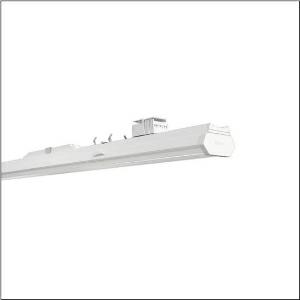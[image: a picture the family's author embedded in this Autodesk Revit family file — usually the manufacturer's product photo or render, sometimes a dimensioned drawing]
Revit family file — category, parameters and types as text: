
# Revit family: licross_21_protected_mo_52td127n485g
name_source: partatom
category: Lighting Fixtures
units: mm (PartAtom-declared; Revit-internal decimal feet)

## family parameters
Cut with Voids When Loaded = No
Host = Face
Light Source = No
Part Type = Normal
Room Calculation Point = No
Round Connector Dimension = Use Diameter
Shared = No

## types (1)
- Licross 21 Protected MO (1 x LED, 8610 lm, 47.9 W, 4000K)
    Apparent Load = 48 VA
    CIE Flux Codes = 73 92 98 99 100
    Color Rendering = 80
    Color Temperature = 4000K
    Default Elevation = 1800 mm
    Description = Licross 21 Protected MO, luminaire insert, of sheet steel, galvanised, coil coated, white, length: 1.500mm, width: 90mm, height: 101mm, LED rated luminous flux: 8.610lm, light colour: 840, SDCM (Standard Deviation of Colour Matching)MacAdam ≤ 3 SDCM (initial), control gear: ON/OFF, with plug, 3-pole, with phase selection, mains connection: 220..240V, AC, 50/60Hz, rated input power: 48W, internal wiring halogen-free, primary light control with lens, of plastic, primary optical cover: cover, of PMMA, light emission: direct distribution, primary light characteristic: symmetric, protection rating (complete): IP54, insulation class (complete): insulation class I (protective earthing), certification: CE, ENEC, VDE, UKCA, protection symbol: D if used in an environment with non-conductive dust loads with corresponding accessories, impact resistance: IK06, permissible ambient temperature for indoor applications: -35..+45°C, corresponds to IFS (International Featured Standards) requirements for safety and quality in the food industry, reducing of maximum allowable ambient temperature of 5°C with ceiling mounting, LABS conformity tested according to VDMA 24364:2018-05, The light source and the operating device comply with the requirements of the Ecodesign Regulation (EU) 2019/2020 and are replaceable in accordance with this regulation, packaging unit: 1 piece
    Height = 92 mm
    Lamp = 1 x LED
    Lamp Light Flux = 8610 lm
    Lamp Power = 47.9 W
    Lamp count = 1
    Length = 1500 mm
    Luminous efficacy = 180 lm/W
    Manufacturer = Siteco
    ModVariant = No
    Model = 52TD127N485G
    Mounting Place = Ceiling
    Mounting Type = Pendant
    Number of Poles = 1
    OnlyDefault = Yes
    Power Factor = 1
    Product Name = Licross 21 Protected MO
    Product group = luminaire insert | ceiling pendant
    ProductGroupID = 901
    Protection Class = Protection class I
    Protection Degree = IP 54
    RLX_Detail_Level = 1
    RLX_Emergency_Light_Flux = 0 lm
    RLX_Emergency_Type = 0
    RLX_Emergency_Type_DB = No
    RlxData = <blob elided: 20949 chars, md5=1563f72c>
    Socket = socket
    Standby Power = 0 W
    System Light Flux = 8610 lm
    System Power = 48 W
    Type Comments = Product without accessories
    Type Image = l_1256148.jpg
    URL = http://relux.com
    VarID = ---
    Voltage = 0 V
    Weight = 0.00 kg
    Width = 88 mm

## geometry (parser evidence)
native form markers: Blend x4, Sweep x11
no freeform markers — native parametric forms only
